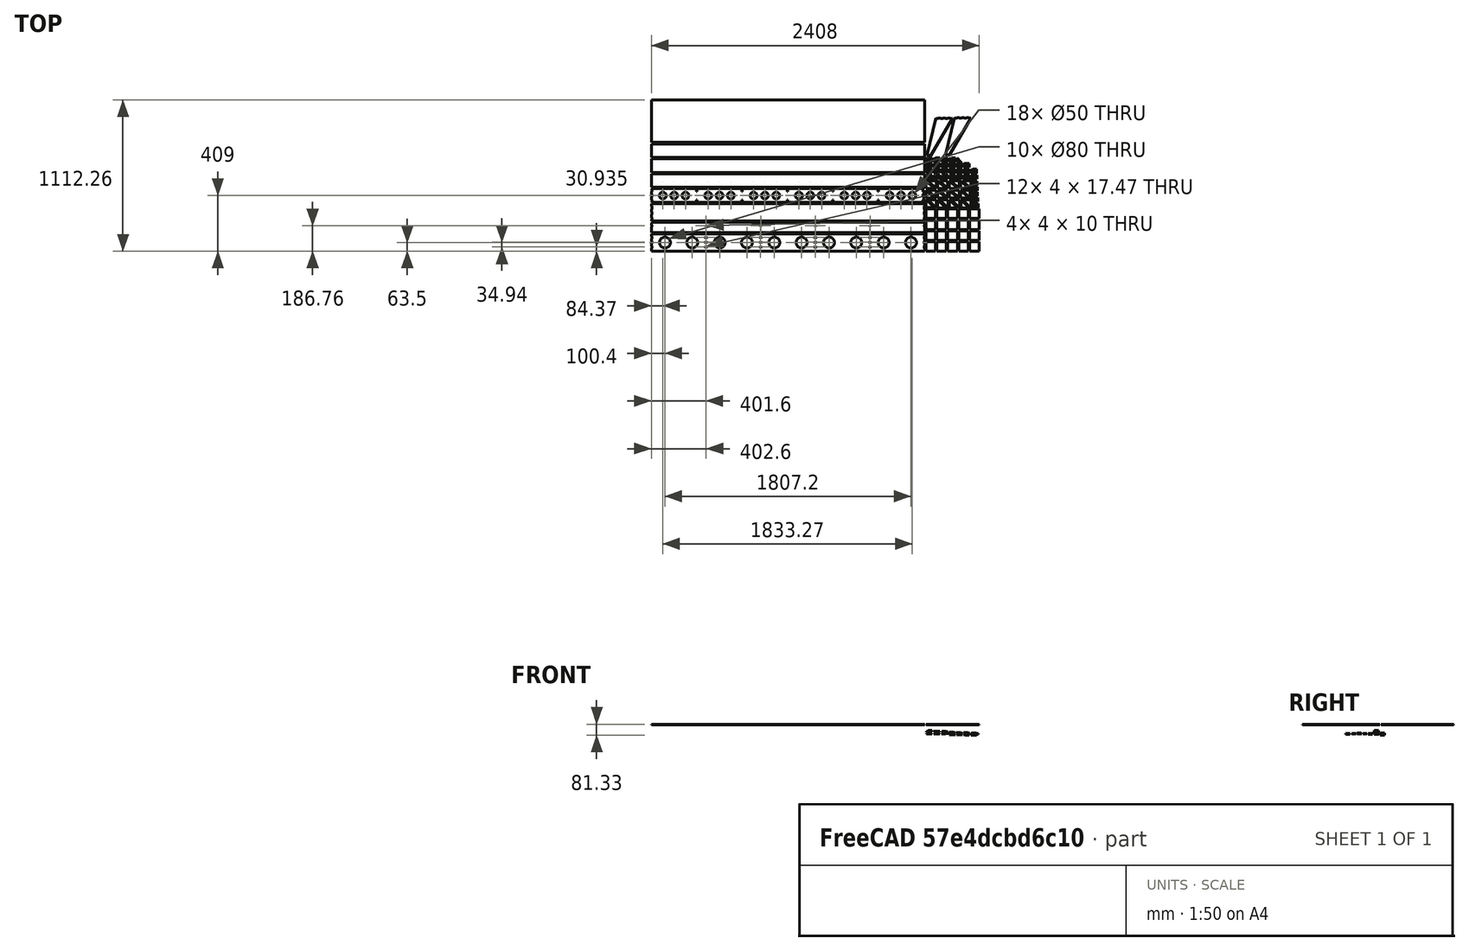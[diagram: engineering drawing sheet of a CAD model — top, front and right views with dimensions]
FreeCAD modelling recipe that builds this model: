
FCSTD DOCUMENT  (FreeCAD 0.19R24291 (Git))
Label: CAM-3
License: All rights reserved
LicenseURL: http://en.wikipedia.org/wiki/All_rights_reserved
objects: Part::Feature×113, Part::Part2DObjectPython×113
note: 226 computed .brp shape members not serialized (recipe doc carries the construction recipe); baked Part::Feature solids carry a one-line shape summary decoded from their .brp

FEATURE [Part::Feature] test
  Placement = pos=(2219,3712,34) rot=(0,1,0;3.14159rad)
  shape: bbox 60 x 60 x 4 mm, 5 faces (baked)
FEATURE [Part::Feature] test001
  Placement = pos=(2150,3712,34) rot=(0,1,0;3.14159rad)
  shape: bbox 60 x 60 x 4 mm, 5 faces (baked)
FEATURE [Part::Feature] test002
  Placement = pos=(2273,3782,34) rot=(0,1,0;3.14159rad)
  shape: bbox 60 x 60 x 4 mm, 5 faces (baked)
FEATURE [Part::Feature] test003
  Placement = pos=(2336,3782,34) rot=(0,1,0;3.14159rad)
  shape: bbox 60 x 60 x 4 mm, 5 faces (baked)
FEATURE [Part::Feature] test004
  Placement = pos=(2290,3852,34) rot=(0,1,0;3.14159rad)
  shape: bbox 60 x 60 x 4 mm, 5 faces (baked)
FEATURE [Part::Feature] test005
  Placement = pos=(2478,3852,34) rot=(0,1,0;3.14159rad)
  shape: bbox 60 x 60 x 4 mm, 5 faces (baked)
FEATURE [Part::Feature] test006
  Placement = pos=(2503,3852,34) rot=(0,1,0;3.14159rad)
  shape: bbox 60 x 60 x 4 mm, 5 faces (baked)
FEATURE [Part::Feature] test011
  Placement = pos=(2824,3712,34) rot=(0,1,0;3.14159rad)
  shape: bbox 60 x 60 x 4 mm, 5 faces (baked)
FEATURE [Part::Feature] test012
  Placement = pos=(3004,3712,34) rot=(0,1,0;3.14159rad)
  shape: bbox 60 x 60 x 4 mm, 5 faces (baked)
FEATURE [Part::Feature] test013
  Placement = pos=(2848,3782,34) rot=(0,1,0;3.14159rad)
  shape: bbox 60 x 60 x 4 mm, 5 faces (baked)
FEATURE [Part::Feature] test014
  Placement = pos=(3213,3782,34) rot=(0,1,0;3.14159rad)
  shape: bbox 60 x 60 x 4 mm, 5 faces (baked)
FEATURE [Part::Feature] test015
  Placement = pos=(3028,3782,34) rot=(0,1,0;3.14159rad)
  shape: bbox 60 x 60 x 4 mm, 5 faces (baked)
FEATURE [Part::Feature] test016
  Placement = pos=(2493,3852,34) rot=(0,1,0;3.14159rad)
  shape: bbox 60 x 60 x 4 mm, 5 faces (baked)
FEATURE [Part::Feature] test017
  Placement = pos=(3323,3852,34) rot=(0,1,0;3.14159rad)
  shape: bbox 60 x 60 x 4 mm, 5 faces (baked)
FEATURE [Part::Feature] test018
  Placement = pos=(3303,3782,34) rot=(0,1,0;3.14159rad)
  shape: bbox 60 x 60 x 4 mm, 5 faces (baked)
FEATURE [Part::Feature] test020
  Placement = pos=(3333,3852,34) rot=(0,1,0;3.14159rad)
  shape: bbox 60 x 60 x 4 mm, 5 faces (baked)
FEATURE [Part::Feature] test021
  Placement = pos=(3528,3852,34) rot=(0,1,0;3.14159rad)
  shape: bbox 60 x 60 x 4 mm, 5 faces (baked)
FEATURE [Part::Feature] test022
  Placement = pos=(3288,3713,34) rot=(0,1,0;3.14159rad)
  shape: bbox 60 x 60 x 4 mm, 5 faces (baked)
FEATURE [Part::Feature] test023
  Placement = pos=(3469,3712,34) rot=(0,1,0;3.14159rad)
  shape: bbox 60 x 60 x 4 mm, 5 faces (baked)
FEATURE [Part::Feature] test024
  Placement = pos=(3654,3712,34) rot=(0,1,0;3.14159rad)
  shape: bbox 60 x 60 x 4 mm, 5 faces (baked)
FEATURE [Part::Feature] test025
  Placement = pos=(3593,3782,34) rot=(0,1,0;3.14159rad)
  shape: bbox 60 x 60 x 4 mm, 5 faces (baked)
FEATURE [Part::Feature] test026
  Placement = pos=(3749,3712,34) rot=(0,1,0;3.14159rad)
  shape: bbox 60 x 60 x 4 mm, 5 faces (baked)
FEATURE [Part::Feature] test027
  Placement = pos=(3788,3852,34) rot=(0,1,0;3.14159rad)
  shape: bbox 60 x 60 x 4 mm, 5 faces (baked)
FEATURE [Part::Feature] test028
  Placement = pos=(3773,3782,34) rot=(0,1,0;3.14159rad)
  shape: bbox 60 x 60 x 4 mm, 5 faces (baked)
FEATURE [Part::Feature] test029
  Placement = pos=(2373,3738,34) rot=(0,1,0;3.14159rad)
  shape: bbox 70 x 70 x 4 mm, 6 faces (baked)
FEATURE [Part::Feature] test030
  Placement = pos=(2373,3598,34) rot=(0,1,0;3.14159rad)
  shape: bbox 70 x 70 x 4 mm, 6 faces (baked)
FEATURE [Part::Feature] test031
  Placement = pos=(2153,3578,34) rot=(0,1,0;3.14159rad)
  shape: bbox 70 x 70 x 4 mm, 6 faces (baked)
FEATURE [Part::Feature] test032
  Placement = pos=(2393,3598,34) rot=(0,1,0;3.14159rad)
  shape: bbox 70 x 70 x 4 mm, 6 faces (baked)
FEATURE [Part::Feature] test033
  Placement = pos=(2493,3578,34) rot=(0,1,0;3.14159rad)
  shape: bbox 70 x 70 x 4 mm, 6 faces (baked)
FEATURE [Part::Feature] test034
  Placement = pos=(2253,3758,34) rot=(0,1,0;3.14159rad)
  shape: bbox 70 x 70 x 4 mm, 6 faces (baked)
FEATURE [Part::Feature] test035
  Placement = pos=(2353,3838,34) rot=(0,1,0;3.14159rad)
  shape: bbox 70 x 70 x 4 mm, 6 faces (baked)
FEATURE [Part::Feature] test036
  Placement = pos=(2433,3738,34) rot=(0,1,0;3.14159rad)
  shape: bbox 70 x 70 x 4 mm, 6 faces (baked)
FEATURE [Part::Feature] test037
  Placement = pos=(2613,3838,34) rot=(0,1,0;3.14159rad)
  shape: bbox 70 x 70 x 4 mm, 6 faces (baked)
FEATURE [Part::Feature] test038
  Placement = pos=(2693,3738,34) rot=(0,1,0;3.14159rad)
  shape: bbox 70 x 70 x 4 mm, 6 faces (baked)
FEATURE [Part::Feature] test039
  Placement = pos=(2873,3578,34) rot=(0,1,0;3.14159rad)
  shape: bbox 70 x 70 x 4 mm, 6 faces (baked)
FEATURE [Part::Feature] test040
  Placement = pos=(2873,3758,34) rot=(0,1,0;3.14159rad)
  shape: bbox 70 x 70 x 4 mm, 6 faces (baked)
FEATURE [Part::Feature] test041
  Placement = pos=(2813,3498,34) rot=(0,1,0;3.14159rad)
  shape: bbox 70 x 70 x 4 mm, 6 faces (baked)
FEATURE [Part::Feature] test042
  Placement = pos=(2733,3598,34) rot=(0,1,0;3.14159rad)
  shape: bbox 70 x 70 x 4 mm, 6 faces (baked)
FEATURE [Part::Feature] test043
  Placement = pos=(2753,3598,34) rot=(0,1,0;3.14159rad)
  shape: bbox 70 x 70 x 4 mm, 6 faces (baked)
FEATURE [Part::Feature] test044
  Placement = pos=(2833,3578,34) rot=(0,1,0;3.14159rad)
  shape: bbox 70 x 70 x 4 mm, 6 faces (baked)
FEATURE [Part::Feature] test045
  Placement = pos=(3013,3678,34) rot=(0,1,0;3.14159rad)
  shape: bbox 70 x 70 x 4 mm, 6 faces (baked)
FEATURE [Part::Feature] test046
  Placement = pos=(2933,3658,34) rot=(0,1,0;3.14159rad)
  shape: bbox 70 x 70 x 4 mm, 6 faces (baked)
FEATURE [Part::Feature] test047
  Placement = pos=(3113,3758,34) rot=(0,1,0;3.14159rad)
  shape: bbox 70 x 70 x 4 mm, 6 faces (baked)
FEATURE [Part::Feature] test048
  Placement = pos=(3193,3658,34) rot=(0,1,0;3.14159rad)
  shape: bbox 70 x 70 x 4 mm, 6 faces (baked)
FEATURE [Part::Feature] test049
  Placement = pos=(2204.93,4207.11,-25.2046) rot=(0,1,0;3.14159rad)
  shape: bbox 30 x 30 x 4 mm, 5 faces (baked)
FEATURE [Part::Feature] test050
  Placement = pos=(2219.52,4207.19,-22.4733) rot=(0,1,0;3.14159rad)
  shape: bbox 30 x 30 x 4 mm, 5 faces (baked)
FEATURE [Part::Feature] test051
  Placement = pos=(2241.29,4206.7,-19.2967) rot=(0,1,0;3.14159rad)
  shape: bbox 30 x 30 x 4 mm, 5 faces (baked)
FEATURE [Part::Feature] test052
  Placement = pos=(2169.36,4207.86,-17.4437) rot=(0,1,0;3.14159rad)
  shape: bbox 30 x 30 x 4 mm, 5 faces (baked)
FEATURE [Part::Feature] test053
  Placement = pos=(2308.6,4207.73,-17.9467) rot=(0,1,0;3.14159rad)
  shape: bbox 30 x 30 x 4 mm, 5 faces (baked)
FEATURE [Part::Feature] test054
  Placement = pos=(2264.57,4207.49,-13.3782) rot=(0,1,0;3.14159rad)
  shape: bbox 30 x 30 x 4 mm, 5 faces (baked)
FEATURE [Part::Feature] test055
  Placement = pos=(2451.48,4252.87,-38.6741) rot=(0,1,0;3.14159rad)
  shape: bbox 30 x 30 x 4 mm, 5 faces (baked)
FEATURE [Part::Feature] test056
  Placement = pos=(2582.06,4251.78,-39.2106) rot=(0,1,0;3.14159rad)
  shape: bbox 30 x 30 x 4 mm, 5 faces (baked)
FEATURE [Part::Feature] test057
  Placement = pos=(2343.78,4293.17,34) rot=(0,1,0;3.14159rad)
  shape: bbox 30 x 30 x 4 mm, 5 faces (baked)
FEATURE [Part::Feature] test058
  Placement = pos=(2552.47,4294.85,34) rot=(0,1,0;3.14159rad)
  shape: bbox 30 x 30 x 4 mm, 5 faces (baked)
FEATURE [Part::Feature] test059
  Placement = pos=(2536.46,4294.85,34) rot=(0,1,0;3.14159rad)
  shape: bbox 30 x 30 x 4 mm, 5 faces (baked)
FEATURE [Part::Feature] test060
  Placement = pos=(2733.13,4294.85,34) rot=(0,1,0;3.14159rad)
  shape: bbox 30 x 30 x 4 mm, 5 faces (baked)
FEATURE [Part::Feature] test061
  Placement = pos=(2503.67,4333.51,34) rot=(0,1,0;3.14159rad)
  shape: bbox 30 x 30 x 4 mm, 5 faces (baked)
FEATURE [Part::Feature] test062
  Placement = pos=(2928.72,3997.69,-35.1689) rot=(0,1,0;3.14159rad)
  shape: bbox 30 x 30 x 4 mm, 5 faces (baked)
FEATURE [Part::Feature] test063
  Placement = pos=(2795.04,4207.57,-30.115) rot=(0,1,0;3.14159rad)
  shape: bbox 30 x 30 x 4 mm, 5 faces (baked)
FEATURE [Part::Feature] test064
  Placement = pos=(2824.34,4206.36,-27.0734) rot=(0,1,0;3.14159rad)
  shape: bbox 30 x 30 x 4 mm, 5 faces (baked)
FEATURE [Part::Feature] test065
  Placement = pos=(2811,4207.49,-26.9938) rot=(0,1,0;3.14159rad)
  shape: bbox 30 x 30 x 4 mm, 5 faces (baked)
FEATURE [Part::Feature] test066
  Placement = pos=(2904.44,4251.13,-39.2664) rot=(0,1,0;3.14159rad)
  shape: bbox 30 x 30 x 4 mm, 5 faces (baked)
FEATURE [Part::Feature] test067
  Placement = pos=(2945.14,4250.68,-41.0286) rot=(0,1,0;3.14159rad)
  shape: bbox 30 x 30 x 4 mm, 5 faces (baked)
FEATURE [Part::Feature] test068
  Placement = pos=(2789.78,4293.94,34) rot=(0,1,0;3.14159rad)
  shape: bbox 30 x 30 x 4 mm, 5 faces (baked)
FEATURE [Part::Feature] test069
  Placement = pos=(2839.32,4295.06,34) rot=(0,1,0;3.14159rad)
  shape: bbox 30 x 30 x 4 mm, 5 faces (baked)
FEATURE [Part::Feature] test070
  Placement = pos=(2973.24,4295.15,34) rot=(0,1,0;3.14159rad)
  shape: bbox 30 x 30 x 4 mm, 5 faces (baked)
FEATURE [Part::Feature] test071
  Placement = pos=(2738.02,4334.55,34) rot=(0,1,0;3.14159rad)
  shape: bbox 30 x 30 x 4 mm, 5 faces (baked)
FEATURE [Part::Feature] test072
  Placement = pos=(2874.75,4334.28,34) rot=(0,1,0;3.14159rad)
  shape: bbox 30 x 30 x 4 mm, 5 faces (baked)
FEATURE [Part::Feature] test073
  Placement = pos=(3224.21,3997.16,-35.6939) rot=(0,1,0;3.14159rad)
  shape: bbox 30 x 30 x 4 mm, 5 faces (baked)
FEATURE [Part::Feature] test074
  Placement = pos=(3236.81,4040.63,-33.7602) rot=(0,1,0;3.14159rad)
  shape: bbox 30 x 30 x 4 mm, 5 faces (baked)
FEATURE [Part::Feature] test075
  Placement = pos=(3242.01,4207.06,-30.7179) rot=(0,1,0;3.14159rad)
  shape: bbox 30 x 30 x 4 mm, 5 faces (baked)
FEATURE [Part::Feature] test076
  Placement = pos=(3255.03,4207.48,-28.8446) rot=(0,1,0;3.14159rad)
  shape: bbox 30 x 30 x 4 mm, 5 faces (baked)
FEATURE [Part::Feature] test077
  Placement = pos=(3258.08,4250.89,-41.0843) rot=(0,1,0;3.14159rad)
  shape: bbox 30 x 30 x 4 mm, 5 faces (baked)
FEATURE [Part::Feature] test078
  Placement = pos=(3390.73,4250.22,-41.5606) rot=(0,1,0;3.14159rad)
  shape: bbox 30 x 30 x 4 mm, 5 faces (baked)
FEATURE [Part::Feature] test079
  Placement = pos=(3387.34,4250.08,-41.5626) rot=(0,1,0;3.14159rad)
  shape: bbox 30 x 30 x 4 mm, 5 faces (baked)
FEATURE [Part::Feature] test080
  Placement = pos=(3193.91,4293.87,34) rot=(0,1,0;3.14159rad)
  shape: bbox 30 x 30 x 4 mm, 5 faces (baked)
FEATURE [Part::Feature] test081
  Placement = pos=(3469.53,4293.98,34) rot=(0,1,0;3.14159rad)
  shape: bbox 30 x 30 x 4 mm, 5 faces (baked)
FEATURE [Part::Feature] test082
  Placement = pos=(3332.54,4334.2,34) rot=(0,1,0;3.14159rad)
  shape: bbox 30 x 30 x 4 mm, 5 faces (baked)
FEATURE [Part::Feature] test083
  Placement = pos=(3333.65,4333.93,34) rot=(0,1,0;3.14159rad)
  shape: bbox 30 x 30 x 4 mm, 5 faces (baked)
FEATURE [Part::Feature] test084
  Placement = pos=(3685.99,4206.94,-35.222) rot=(0,1,0;3.14159rad)
  shape: bbox 30 x 30 x 4 mm, 5 faces (baked)
FEATURE [Part::Feature] test085
  Placement = pos=(3635.07,4123.66,-33.6609) rot=(0,1,0;3.14159rad)
  shape: bbox 30 x 30 x 4 mm, 5 faces (baked)
FEATURE [Part::Feature] test086
  Placement = pos=(3773.24,4041.85,-32.8391) rot=(0,1,0;3.14159rad)
  shape: bbox 30 x 30 x 4 mm, 5 faces (baked)
FEATURE [Part::Feature] test087
  Placement = pos=(3715.39,4080.71,-31.029) rot=(0,1,0;3.14159rad)
  shape: bbox 30 x 30 x 4 mm, 5 faces (baked)
FEATURE [Part::Feature] test088
  Placement = pos=(3459.34,4251.87,-32.9911) rot=(0,1,0;3.14159rad)
  shape: bbox 30 x 30 x 4 mm, 5 faces (baked)
FEATURE [Part::Feature] test089
  Placement = pos=(3844.41,4251.11,-43.3309) rot=(0,1,0;3.14159rad)
  shape: bbox 30 x 30 x 4 mm, 5 faces (baked)
FEATURE [Part::Feature] test090
  Placement = pos=(3538.86,4293.21,34) rot=(0,1,0;3.14159rad)
  shape: bbox 30 x 30 x 4 mm, 5 faces (baked)
FEATURE [Part::Feature] test091
  Placement = pos=(3818.42,4295.56,34) rot=(0,1,0;3.14159rad)
  shape: bbox 30 x 30 x 4 mm, 5 faces (baked)
FEATURE [Part::Feature] test092
  Placement = pos=(3894.39,4294.26,34) rot=(0,1,0;3.14159rad)
  shape: bbox 30 x 30 x 4 mm, 5 faces (baked)
FEATURE [Part::Feature] test093
  Placement = pos=(3850.15,4332.35,34) rot=(0,1,0;3.14159rad)
  shape: bbox 30 x 30 x 4 mm, 5 faces (baked)
FEATURE [Part::Feature] test094
  Placement = pos=(3869.81,4333.35,34) rot=(0,1,0;3.14159rad)
  shape: bbox 30 x 30 x 4 mm, 5 faces (baked)
FEATURE [Part::Feature] test095
  Placement = pos=(4086.62,4161.95,-35.224) rot=(0,1,0;3.14159rad)
  shape: bbox 30 x 30 x 4 mm, 5 faces (baked)
FEATURE [Part::Feature] test096
  Placement = pos=(4108.86,4207.4,-33.482) rot=(0,1,0;3.14159rad)
  shape: bbox 30 x 30 x 4 mm, 5 faces (baked)
FEATURE [Part::Feature] test097
  Placement = pos=(4170.9,4082.98,-32.7595) rot=(0,1,0;3.14159rad)
  shape: bbox 30 x 30 x 4 mm, 5 faces (baked)
FEATURE [Part::Feature] test098
  Placement = pos=(3859.82,4207.89,-19.66) rot=(0,1,0;3.14159rad)
  shape: bbox 30 x 30 x 4 mm, 5 faces (baked)
FEATURE [Part::Feature] test099
  Placement = pos=(3918.28,4251.35,-33.5551) rot=(0,1,0;3.14159rad)
  shape: bbox 30 x 30 x 4 mm, 5 faces (baked)
FEATURE [Part::Feature] test100
  Placement = pos=(3993.95,4252.01,-33.5112) rot=(0,1,0;3.14159rad)
  shape: bbox 30 x 30 x 4 mm, 5 faces (baked)
FEATURE [Part::Feature] test101
  Placement = pos=(4055.01,4252.2,-32.7736) rot=(0,1,0;3.14159rad)
  shape: bbox 30 x 30 x 4 mm, 5 faces (baked)
FEATURE [Part::Feature] test102
  Placement = pos=(4131.15,4253.38,-32.811) rot=(0,1,0;3.14159rad)
  shape: bbox 30 x 30 x 4 mm, 5 faces (baked)
FEATURE [Part::Feature] test103
  Placement = pos=(4191.09,4333.78,34) rot=(0,1,0;3.14159rad)
  shape: bbox 30 x 30 x 4 mm, 5 faces (baked)
FEATURE [Part::Feature] test104
  Placement = pos=(4271.05,4253.08,-30.6289) rot=(0,1,0;3.14159rad)
  shape: bbox 30 x 30 x 4 mm, 5 faces (baked)
FEATURE [Part::Feature] test105
  Placement = pos=(4326.29,4333.18,34) rot=(0,1,0;3.14159rad)
  shape: bbox 30 x 30 x 4 mm, 5 faces (baked)
FEATURE [Part::Feature] test106
  Placement = pos=(4514.02,4161.12,-35.008) rot=(0,1,0;3.14159rad)
  shape: bbox 30 x 30 x 4 mm, 5 faces (baked)
FEATURE [Part::Feature] test107
  Placement = pos=(4569.29,4122.33,-34.048) rot=(0,1,0;3.14159rad)
  shape: bbox 30 x 30 x 4 mm, 5 faces (baked)
FEATURE [Part::Feature] test108
  Placement = pos=(2009,4502,34) rot=(0,1,0;3.14159rad)
  shape: bbox 2008 x 100 x 4 mm, 6 faces (baked)
FEATURE [Part::Feature] test109
  Placement = pos=(2009,4392,34) rot=(0,1,0;3.14159rad)
  shape: bbox 2008 x 100 x 4 mm, 6 faces (baked)
FEATURE [Part::Feature] test110
  Placement = pos=(2009,4612,34) rot=(0,1,0;3.14159rad)
  shape: bbox 2008 x 100 x 4 mm, 6 faces (baked)
FEATURE [Part::Feature] test111
  Placement = pos=(1001,1059,-268) rot=(1,0,0;1.5708rad)
  shape: bbox 2000 x 100 x 4 mm, 80 faces (baked)
FEATURE [Part::Feature] test112
  Placement = pos=(1005,947,634) rot=(1,0,0;1.5708rad)
  shape: bbox 2008 x 127 x 4 mm, 30 faces (baked)
FEATURE [Part::Feature] test113
  Placement = pos=(2142.38,2233.25,-970) rot=(0,1,0;1.5708rad)
  shape: bbox 187.7 x 277.1 x 4 mm, 23 faces (baked)
FEATURE [Part::Feature] test114
  Placement = pos=(1004,725,638) rot=(1,0,0;1.5708rad)
  shape: bbox 2008 x 127 x 4 mm, 88 faces (baked)
FEATURE [Part::Feature] test115
  Placement = pos=(2279.6,2235.36,1034) rot=(0,1,0;1.5708rad)
  shape: bbox 187.7 x 277.1 x 4 mm, 23 faces (baked)
FEATURE [Part::Feature] test120
  Placement = pos=(1005,959,396.842) rot=(1,0,0;2.61799rad)
  shape: bbox 2008 x 313 x 4 mm, 6 faces (baked)
FEATURE [Part::Feature] test121
  Placement = pos=(1005,742,911.1) rot=(1,0,0;1.5708rad)
  shape: bbox 2008 x 74.7 x 4 mm, 50 faces (baked)
FEATURE [Part::Part2DObjectPython] Shape2DView  # Draft 2D object (typed FeaturePython)
  Base = -> test
  FuseArch = false
  HiddenLines = false
  InPlace = true
  Projection = (0,0,1)
  ProjectionMode = 0
  SegmentLength = 0.05
  Tessellation = false
  VisibleOnly = false
FEATURE [Part::Part2DObjectPython] Shape2DView001  # Draft 2D object (typed FeaturePython)
  Base = -> test001
  FuseArch = false
  HiddenLines = false
  InPlace = true
  Projection = (0,0,1)
  ProjectionMode = 0
  SegmentLength = 0.05
  Tessellation = false
  VisibleOnly = false
FEATURE [Part::Part2DObjectPython] Shape2DView002  # Draft 2D object (typed FeaturePython)
  Base = -> test002
  FuseArch = false
  HiddenLines = false
  InPlace = true
  Projection = (0,0,1)
  ProjectionMode = 0
  SegmentLength = 0.05
  Tessellation = false
  VisibleOnly = false
FEATURE [Part::Part2DObjectPython] Shape2DView003  # Draft 2D object (typed FeaturePython)
  Base = -> test003
  FuseArch = false
  HiddenLines = false
  InPlace = true
  Projection = (0,0,1)
  ProjectionMode = 0
  SegmentLength = 0.05
  Tessellation = false
  VisibleOnly = false
FEATURE [Part::Part2DObjectPython] Shape2DView004  # Draft 2D object (typed FeaturePython)
  Base = -> test004
  FuseArch = false
  HiddenLines = false
  InPlace = true
  Projection = (0,0,1)
  ProjectionMode = 0
  SegmentLength = 0.05
  Tessellation = false
  VisibleOnly = false
FEATURE [Part::Part2DObjectPython] Shape2DView005  # Draft 2D object (typed FeaturePython)
  Base = -> test005
  FuseArch = false
  HiddenLines = false
  InPlace = true
  Projection = (0,0,1)
  ProjectionMode = 0
  SegmentLength = 0.05
  Tessellation = false
  VisibleOnly = false
FEATURE [Part::Part2DObjectPython] Shape2DView006  # Draft 2D object (typed FeaturePython)
  Base = -> test006
  FuseArch = false
  HiddenLines = false
  InPlace = true
  Projection = (0,0,1)
  ProjectionMode = 0
  SegmentLength = 0.05
  Tessellation = false
  VisibleOnly = false
FEATURE [Part::Part2DObjectPython] Shape2DView011  # Draft 2D object (typed FeaturePython)
  Base = -> test011
  FuseArch = false
  HiddenLines = false
  InPlace = true
  Projection = (0,0,1)
  ProjectionMode = 0
  SegmentLength = 0.05
  Tessellation = false
  VisibleOnly = false
FEATURE [Part::Part2DObjectPython] Shape2DView012  # Draft 2D object (typed FeaturePython)
  Base = -> test012
  FuseArch = false
  HiddenLines = false
  InPlace = true
  Projection = (0,0,1)
  ProjectionMode = 0
  SegmentLength = 0.05
  Tessellation = false
  VisibleOnly = false
FEATURE [Part::Part2DObjectPython] Shape2DView013  # Draft 2D object (typed FeaturePython)
  Base = -> test013
  FuseArch = false
  HiddenLines = false
  InPlace = true
  Projection = (0,0,1)
  ProjectionMode = 0
  SegmentLength = 0.05
  Tessellation = false
  VisibleOnly = false
FEATURE [Part::Part2DObjectPython] Shape2DView014  # Draft 2D object (typed FeaturePython)
  Base = -> test014
  FuseArch = false
  HiddenLines = false
  InPlace = true
  Projection = (0,0,1)
  ProjectionMode = 0
  SegmentLength = 0.05
  Tessellation = false
  VisibleOnly = false
FEATURE [Part::Part2DObjectPython] Shape2DView015  # Draft 2D object (typed FeaturePython)
  Base = -> test015
  FuseArch = false
  HiddenLines = false
  InPlace = true
  Projection = (0,0,1)
  ProjectionMode = 0
  SegmentLength = 0.05
  Tessellation = false
  VisibleOnly = false
FEATURE [Part::Part2DObjectPython] Shape2DView016  # Draft 2D object (typed FeaturePython)
  Base = -> test016
  FuseArch = false
  HiddenLines = false
  InPlace = true
  Projection = (0,0,1)
  ProjectionMode = 0
  SegmentLength = 0.05
  Tessellation = false
  VisibleOnly = false
FEATURE [Part::Part2DObjectPython] Shape2DView017  # Draft 2D object (typed FeaturePython)
  Base = -> test017
  FuseArch = false
  HiddenLines = false
  InPlace = true
  Projection = (0,0,1)
  ProjectionMode = 0
  SegmentLength = 0.05
  Tessellation = false
  VisibleOnly = false
FEATURE [Part::Part2DObjectPython] Shape2DView018  # Draft 2D object (typed FeaturePython)
  Base = -> test018
  FuseArch = false
  HiddenLines = false
  InPlace = true
  Projection = (0,0,1)
  ProjectionMode = 0
  SegmentLength = 0.05
  Tessellation = false
  VisibleOnly = false
FEATURE [Part::Part2DObjectPython] Shape2DView020  # Draft 2D object (typed FeaturePython)
  Base = -> test020
  FuseArch = false
  HiddenLines = false
  InPlace = true
  Projection = (0,0,1)
  ProjectionMode = 0
  SegmentLength = 0.05
  Tessellation = false
  VisibleOnly = false
FEATURE [Part::Part2DObjectPython] Shape2DView021  # Draft 2D object (typed FeaturePython)
  Base = -> test021
  FuseArch = false
  HiddenLines = false
  InPlace = true
  Projection = (0,0,1)
  ProjectionMode = 0
  SegmentLength = 0.05
  Tessellation = false
  VisibleOnly = false
FEATURE [Part::Part2DObjectPython] Shape2DView022  # Draft 2D object (typed FeaturePython)
  Base = -> test022
  FuseArch = false
  HiddenLines = false
  InPlace = true
  Projection = (0,0,1)
  ProjectionMode = 0
  SegmentLength = 0.05
  Tessellation = false
  VisibleOnly = false
FEATURE [Part::Part2DObjectPython] Shape2DView023  # Draft 2D object (typed FeaturePython)
  Base = -> test023
  FuseArch = false
  HiddenLines = false
  InPlace = true
  Projection = (0,0,1)
  ProjectionMode = 0
  SegmentLength = 0.05
  Tessellation = false
  VisibleOnly = false
FEATURE [Part::Part2DObjectPython] Shape2DView024  # Draft 2D object (typed FeaturePython)
  Base = -> test024
  FuseArch = false
  HiddenLines = false
  InPlace = true
  Projection = (0,0,1)
  ProjectionMode = 0
  SegmentLength = 0.05
  Tessellation = false
  VisibleOnly = false
FEATURE [Part::Part2DObjectPython] Shape2DView025  # Draft 2D object (typed FeaturePython)
  Base = -> test025
  FuseArch = false
  HiddenLines = false
  InPlace = true
  Projection = (0,0,1)
  ProjectionMode = 0
  SegmentLength = 0.05
  Tessellation = false
  VisibleOnly = false
FEATURE [Part::Part2DObjectPython] Shape2DView026  # Draft 2D object (typed FeaturePython)
  Base = -> test026
  FuseArch = false
  HiddenLines = false
  InPlace = true
  Projection = (0,0,1)
  ProjectionMode = 0
  SegmentLength = 0.05
  Tessellation = false
  VisibleOnly = false
FEATURE [Part::Part2DObjectPython] Shape2DView027  # Draft 2D object (typed FeaturePython)
  Base = -> test027
  FuseArch = false
  HiddenLines = false
  InPlace = true
  Projection = (0,0,1)
  ProjectionMode = 0
  SegmentLength = 0.05
  Tessellation = false
  VisibleOnly = false
FEATURE [Part::Part2DObjectPython] Shape2DView028  # Draft 2D object (typed FeaturePython)
  Base = -> test028
  FuseArch = false
  HiddenLines = false
  InPlace = true
  Projection = (0,0,1)
  ProjectionMode = 0
  SegmentLength = 0.05
  Tessellation = false
  VisibleOnly = false
FEATURE [Part::Part2DObjectPython] Shape2DView029  # Draft 2D object (typed FeaturePython)
  Base = -> test029
  FuseArch = false
  HiddenLines = false
  InPlace = true
  Projection = (0,0,1)
  ProjectionMode = 0
  SegmentLength = 0.05
  Tessellation = false
  VisibleOnly = false
FEATURE [Part::Part2DObjectPython] Shape2DView030  # Draft 2D object (typed FeaturePython)
  Base = -> test030
  FuseArch = false
  HiddenLines = false
  InPlace = true
  Projection = (0,0,1)
  ProjectionMode = 0
  SegmentLength = 0.05
  Tessellation = false
  VisibleOnly = false
FEATURE [Part::Part2DObjectPython] Shape2DView031  # Draft 2D object (typed FeaturePython)
  Base = -> test031
  FuseArch = false
  HiddenLines = false
  InPlace = true
  Projection = (0,0,1)
  ProjectionMode = 0
  SegmentLength = 0.05
  Tessellation = false
  VisibleOnly = false
FEATURE [Part::Part2DObjectPython] Shape2DView032  # Draft 2D object (typed FeaturePython)
  Base = -> test032
  FuseArch = false
  HiddenLines = false
  InPlace = true
  Projection = (0,0,1)
  ProjectionMode = 0
  SegmentLength = 0.05
  Tessellation = false
  VisibleOnly = false
FEATURE [Part::Part2DObjectPython] Shape2DView033  # Draft 2D object (typed FeaturePython)
  Base = -> test033
  FuseArch = false
  HiddenLines = false
  InPlace = true
  Projection = (0,0,1)
  ProjectionMode = 0
  SegmentLength = 0.05
  Tessellation = false
  VisibleOnly = false
FEATURE [Part::Part2DObjectPython] Shape2DView034  # Draft 2D object (typed FeaturePython)
  Base = -> test034
  FuseArch = false
  HiddenLines = false
  InPlace = true
  Projection = (0,0,1)
  ProjectionMode = 0
  SegmentLength = 0.05
  Tessellation = false
  VisibleOnly = false
FEATURE [Part::Part2DObjectPython] Shape2DView035  # Draft 2D object (typed FeaturePython)
  Base = -> test035
  FuseArch = false
  HiddenLines = false
  InPlace = true
  Projection = (0,0,1)
  ProjectionMode = 0
  SegmentLength = 0.05
  Tessellation = false
  VisibleOnly = false
FEATURE [Part::Part2DObjectPython] Shape2DView036  # Draft 2D object (typed FeaturePython)
  Base = -> test036
  FuseArch = false
  HiddenLines = false
  InPlace = true
  Projection = (0,0,1)
  ProjectionMode = 0
  SegmentLength = 0.05
  Tessellation = false
  VisibleOnly = false
FEATURE [Part::Part2DObjectPython] Shape2DView037  # Draft 2D object (typed FeaturePython)
  Base = -> test037
  FuseArch = false
  HiddenLines = false
  InPlace = true
  Projection = (0,0,1)
  ProjectionMode = 0
  SegmentLength = 0.05
  Tessellation = false
  VisibleOnly = false
FEATURE [Part::Part2DObjectPython] Shape2DView038  # Draft 2D object (typed FeaturePython)
  Base = -> test038
  FuseArch = false
  HiddenLines = false
  InPlace = true
  Projection = (0,0,1)
  ProjectionMode = 0
  SegmentLength = 0.05
  Tessellation = false
  VisibleOnly = false
FEATURE [Part::Part2DObjectPython] Shape2DView039  # Draft 2D object (typed FeaturePython)
  Base = -> test039
  FuseArch = false
  HiddenLines = false
  InPlace = true
  Projection = (0,0,1)
  ProjectionMode = 0
  SegmentLength = 0.05
  Tessellation = false
  VisibleOnly = false
FEATURE [Part::Part2DObjectPython] Shape2DView040  # Draft 2D object (typed FeaturePython)
  Base = -> test040
  FuseArch = false
  HiddenLines = false
  InPlace = true
  Projection = (0,0,1)
  ProjectionMode = 0
  SegmentLength = 0.05
  Tessellation = false
  VisibleOnly = false
FEATURE [Part::Part2DObjectPython] Shape2DView041  # Draft 2D object (typed FeaturePython)
  Base = -> test041
  FuseArch = false
  HiddenLines = false
  InPlace = true
  Projection = (0,0,1)
  ProjectionMode = 0
  SegmentLength = 0.05
  Tessellation = false
  VisibleOnly = false
FEATURE [Part::Part2DObjectPython] Shape2DView042  # Draft 2D object (typed FeaturePython)
  Base = -> test042
  FuseArch = false
  HiddenLines = false
  InPlace = true
  Projection = (0,0,1)
  ProjectionMode = 0
  SegmentLength = 0.05
  Tessellation = false
  VisibleOnly = false
FEATURE [Part::Part2DObjectPython] Shape2DView043  # Draft 2D object (typed FeaturePython)
  Base = -> test043
  FuseArch = false
  HiddenLines = false
  InPlace = true
  Projection = (0,0,1)
  ProjectionMode = 0
  SegmentLength = 0.05
  Tessellation = false
  VisibleOnly = false
FEATURE [Part::Part2DObjectPython] Shape2DView044  # Draft 2D object (typed FeaturePython)
  Base = -> test044
  FuseArch = false
  HiddenLines = false
  InPlace = true
  Projection = (0,0,1)
  ProjectionMode = 0
  SegmentLength = 0.05
  Tessellation = false
  VisibleOnly = false
FEATURE [Part::Part2DObjectPython] Shape2DView045  # Draft 2D object (typed FeaturePython)
  Base = -> test045
  FuseArch = false
  HiddenLines = false
  InPlace = true
  Projection = (0,0,1)
  ProjectionMode = 0
  SegmentLength = 0.05
  Tessellation = false
  VisibleOnly = false
FEATURE [Part::Part2DObjectPython] Shape2DView046  # Draft 2D object (typed FeaturePython)
  Base = -> test046
  FuseArch = false
  HiddenLines = false
  InPlace = true
  Projection = (0,0,1)
  ProjectionMode = 0
  SegmentLength = 0.05
  Tessellation = false
  VisibleOnly = false
FEATURE [Part::Part2DObjectPython] Shape2DView047  # Draft 2D object (typed FeaturePython)
  Base = -> test047
  FuseArch = false
  HiddenLines = false
  InPlace = true
  Projection = (0,0,1)
  ProjectionMode = 0
  SegmentLength = 0.05
  Tessellation = false
  VisibleOnly = false
FEATURE [Part::Part2DObjectPython] Shape2DView048  # Draft 2D object (typed FeaturePython)
  Base = -> test048
  FuseArch = false
  HiddenLines = false
  InPlace = true
  Projection = (0,0,1)
  ProjectionMode = 0
  SegmentLength = 0.05
  Tessellation = false
  VisibleOnly = false
FEATURE [Part::Part2DObjectPython] Shape2DView049  # Draft 2D object (typed FeaturePython)
  Base = -> test049
  FuseArch = false
  HiddenLines = false
  InPlace = true
  Projection = (0,0,1)
  ProjectionMode = 0
  SegmentLength = 0.05
  Tessellation = false
  VisibleOnly = false
FEATURE [Part::Part2DObjectPython] Shape2DView050  # Draft 2D object (typed FeaturePython)
  Base = -> test050
  FuseArch = false
  HiddenLines = false
  InPlace = true
  Projection = (0,0,1)
  ProjectionMode = 0
  SegmentLength = 0.05
  Tessellation = false
  VisibleOnly = false
FEATURE [Part::Part2DObjectPython] Shape2DView051  # Draft 2D object (typed FeaturePython)
  Base = -> test051
  FuseArch = false
  HiddenLines = false
  InPlace = true
  Projection = (0,0,1)
  ProjectionMode = 0
  SegmentLength = 0.05
  Tessellation = false
  VisibleOnly = false
FEATURE [Part::Part2DObjectPython] Shape2DView052  # Draft 2D object (typed FeaturePython)
  Base = -> test052
  FuseArch = false
  HiddenLines = false
  InPlace = true
  Projection = (0,0,1)
  ProjectionMode = 0
  SegmentLength = 0.05
  Tessellation = false
  VisibleOnly = false
FEATURE [Part::Part2DObjectPython] Shape2DView053  # Draft 2D object (typed FeaturePython)
  Base = -> test053
  FuseArch = false
  HiddenLines = false
  InPlace = true
  Projection = (0,0,1)
  ProjectionMode = 0
  SegmentLength = 0.05
  Tessellation = false
  VisibleOnly = false
FEATURE [Part::Part2DObjectPython] Shape2DView054  # Draft 2D object (typed FeaturePython)
  Base = -> test054
  FuseArch = false
  HiddenLines = false
  InPlace = true
  Projection = (0,0,1)
  ProjectionMode = 0
  SegmentLength = 0.05
  Tessellation = false
  VisibleOnly = false
FEATURE [Part::Part2DObjectPython] Shape2DView055  # Draft 2D object (typed FeaturePython)
  Base = -> test055
  FuseArch = false
  HiddenLines = false
  InPlace = true
  Projection = (0,0,1)
  ProjectionMode = 0
  SegmentLength = 0.05
  Tessellation = false
  VisibleOnly = false
FEATURE [Part::Part2DObjectPython] Shape2DView056  # Draft 2D object (typed FeaturePython)
  Base = -> test056
  FuseArch = false
  HiddenLines = false
  InPlace = true
  Projection = (0,0,1)
  ProjectionMode = 0
  SegmentLength = 0.05
  Tessellation = false
  VisibleOnly = false
FEATURE [Part::Part2DObjectPython] Shape2DView057  # Draft 2D object (typed FeaturePython)
  Base = -> test057
  FuseArch = false
  HiddenLines = false
  InPlace = true
  Projection = (0,0,1)
  ProjectionMode = 0
  SegmentLength = 0.05
  Tessellation = false
  VisibleOnly = false
FEATURE [Part::Part2DObjectPython] Shape2DView058  # Draft 2D object (typed FeaturePython)
  Base = -> test058
  FuseArch = false
  HiddenLines = false
  InPlace = true
  Projection = (0,0,1)
  ProjectionMode = 0
  SegmentLength = 0.05
  Tessellation = false
  VisibleOnly = false
FEATURE [Part::Part2DObjectPython] Shape2DView059  # Draft 2D object (typed FeaturePython)
  Base = -> test059
  FuseArch = false
  HiddenLines = false
  InPlace = true
  Projection = (0,0,1)
  ProjectionMode = 0
  SegmentLength = 0.05
  Tessellation = false
  VisibleOnly = false
FEATURE [Part::Part2DObjectPython] Shape2DView060  # Draft 2D object (typed FeaturePython)
  Base = -> test060
  FuseArch = false
  HiddenLines = false
  InPlace = true
  Projection = (0,0,1)
  ProjectionMode = 0
  SegmentLength = 0.05
  Tessellation = false
  VisibleOnly = false
FEATURE [Part::Part2DObjectPython] Shape2DView061  # Draft 2D object (typed FeaturePython)
  Base = -> test061
  FuseArch = false
  HiddenLines = false
  InPlace = true
  Projection = (0,0,1)
  ProjectionMode = 0
  SegmentLength = 0.05
  Tessellation = false
  VisibleOnly = false
FEATURE [Part::Part2DObjectPython] Shape2DView062  # Draft 2D object (typed FeaturePython)
  Base = -> test062
  FuseArch = false
  HiddenLines = false
  InPlace = true
  Projection = (0,0,1)
  ProjectionMode = 0
  SegmentLength = 0.05
  Tessellation = false
  VisibleOnly = false
FEATURE [Part::Part2DObjectPython] Shape2DView063  # Draft 2D object (typed FeaturePython)
  Base = -> test063
  FuseArch = false
  HiddenLines = false
  InPlace = true
  Projection = (0,0,1)
  ProjectionMode = 0
  SegmentLength = 0.05
  Tessellation = false
  VisibleOnly = false
FEATURE [Part::Part2DObjectPython] Shape2DView064  # Draft 2D object (typed FeaturePython)
  Base = -> test064
  FuseArch = false
  HiddenLines = false
  InPlace = true
  Projection = (0,0,1)
  ProjectionMode = 0
  SegmentLength = 0.05
  Tessellation = false
  VisibleOnly = false
FEATURE [Part::Part2DObjectPython] Shape2DView065  # Draft 2D object (typed FeaturePython)
  Base = -> test065
  FuseArch = false
  HiddenLines = false
  InPlace = true
  Projection = (0,0,1)
  ProjectionMode = 0
  SegmentLength = 0.05
  Tessellation = false
  VisibleOnly = false
FEATURE [Part::Part2DObjectPython] Shape2DView066  # Draft 2D object (typed FeaturePython)
  Base = -> test066
  FuseArch = false
  HiddenLines = false
  InPlace = true
  Projection = (0,0,1)
  ProjectionMode = 0
  SegmentLength = 0.05
  Tessellation = false
  VisibleOnly = false
FEATURE [Part::Part2DObjectPython] Shape2DView067  # Draft 2D object (typed FeaturePython)
  Base = -> test067
  FuseArch = false
  HiddenLines = false
  InPlace = true
  Projection = (0,0,1)
  ProjectionMode = 0
  SegmentLength = 0.05
  Tessellation = false
  VisibleOnly = false
FEATURE [Part::Part2DObjectPython] Shape2DView068  # Draft 2D object (typed FeaturePython)
  Base = -> test068
  FuseArch = false
  HiddenLines = false
  InPlace = true
  Projection = (0,0,1)
  ProjectionMode = 0
  SegmentLength = 0.05
  Tessellation = false
  VisibleOnly = false
FEATURE [Part::Part2DObjectPython] Shape2DView069  # Draft 2D object (typed FeaturePython)
  Base = -> test069
  FuseArch = false
  HiddenLines = false
  InPlace = true
  Projection = (0,0,1)
  ProjectionMode = 0
  SegmentLength = 0.05
  Tessellation = false
  VisibleOnly = false
FEATURE [Part::Part2DObjectPython] Shape2DView070  # Draft 2D object (typed FeaturePython)
  Base = -> test070
  FuseArch = false
  HiddenLines = false
  InPlace = true
  Projection = (0,0,1)
  ProjectionMode = 0
  SegmentLength = 0.05
  Tessellation = false
  VisibleOnly = false
FEATURE [Part::Part2DObjectPython] Shape2DView071  # Draft 2D object (typed FeaturePython)
  Base = -> test071
  FuseArch = false
  HiddenLines = false
  InPlace = true
  Projection = (0,0,1)
  ProjectionMode = 0
  SegmentLength = 0.05
  Tessellation = false
  VisibleOnly = false
FEATURE [Part::Part2DObjectPython] Shape2DView072  # Draft 2D object (typed FeaturePython)
  Base = -> test072
  FuseArch = false
  HiddenLines = false
  InPlace = true
  Projection = (0,0,1)
  ProjectionMode = 0
  SegmentLength = 0.05
  Tessellation = false
  VisibleOnly = false
FEATURE [Part::Part2DObjectPython] Shape2DView073  # Draft 2D object (typed FeaturePython)
  Base = -> test073
  FuseArch = false
  HiddenLines = false
  InPlace = true
  Projection = (0,0,1)
  ProjectionMode = 0
  SegmentLength = 0.05
  Tessellation = false
  VisibleOnly = false
FEATURE [Part::Part2DObjectPython] Shape2DView074  # Draft 2D object (typed FeaturePython)
  Base = -> test074
  FuseArch = false
  HiddenLines = false
  InPlace = true
  Projection = (0,0,1)
  ProjectionMode = 0
  SegmentLength = 0.05
  Tessellation = false
  VisibleOnly = false
FEATURE [Part::Part2DObjectPython] Shape2DView075  # Draft 2D object (typed FeaturePython)
  Base = -> test075
  FuseArch = false
  HiddenLines = false
  InPlace = true
  Projection = (0,0,1)
  ProjectionMode = 0
  SegmentLength = 0.05
  Tessellation = false
  VisibleOnly = false
FEATURE [Part::Part2DObjectPython] Shape2DView076  # Draft 2D object (typed FeaturePython)
  Base = -> test076
  FuseArch = false
  HiddenLines = false
  InPlace = true
  Projection = (0,0,1)
  ProjectionMode = 0
  SegmentLength = 0.05
  Tessellation = false
  VisibleOnly = false
FEATURE [Part::Part2DObjectPython] Shape2DView077  # Draft 2D object (typed FeaturePython)
  Base = -> test077
  FuseArch = false
  HiddenLines = false
  InPlace = true
  Projection = (0,0,1)
  ProjectionMode = 0
  SegmentLength = 0.05
  Tessellation = false
  VisibleOnly = false
FEATURE [Part::Part2DObjectPython] Shape2DView078  # Draft 2D object (typed FeaturePython)
  Base = -> test078
  FuseArch = false
  HiddenLines = false
  InPlace = true
  Projection = (0,0,1)
  ProjectionMode = 0
  SegmentLength = 0.05
  Tessellation = false
  VisibleOnly = false
FEATURE [Part::Part2DObjectPython] Shape2DView079  # Draft 2D object (typed FeaturePython)
  Base = -> test079
  FuseArch = false
  HiddenLines = false
  InPlace = true
  Projection = (0,0,1)
  ProjectionMode = 0
  SegmentLength = 0.05
  Tessellation = false
  VisibleOnly = false
FEATURE [Part::Part2DObjectPython] Shape2DView080  # Draft 2D object (typed FeaturePython)
  Base = -> test080
  FuseArch = false
  HiddenLines = false
  InPlace = true
  Projection = (0,0,1)
  ProjectionMode = 0
  SegmentLength = 0.05
  Tessellation = false
  VisibleOnly = false
FEATURE [Part::Part2DObjectPython] Shape2DView081  # Draft 2D object (typed FeaturePython)
  Base = -> test081
  FuseArch = false
  HiddenLines = false
  InPlace = true
  Projection = (0,0,1)
  ProjectionMode = 0
  SegmentLength = 0.05
  Tessellation = false
  VisibleOnly = false
FEATURE [Part::Part2DObjectPython] Shape2DView082  # Draft 2D object (typed FeaturePython)
  Base = -> test082
  FuseArch = false
  HiddenLines = false
  InPlace = true
  Projection = (0,0,1)
  ProjectionMode = 0
  SegmentLength = 0.05
  Tessellation = false
  VisibleOnly = false
FEATURE [Part::Part2DObjectPython] Shape2DView083  # Draft 2D object (typed FeaturePython)
  Base = -> test083
  FuseArch = false
  HiddenLines = false
  InPlace = true
  Projection = (0,0,1)
  ProjectionMode = 0
  SegmentLength = 0.05
  Tessellation = false
  VisibleOnly = false
FEATURE [Part::Part2DObjectPython] Shape2DView084  # Draft 2D object (typed FeaturePython)
  Base = -> test084
  FuseArch = false
  HiddenLines = false
  InPlace = true
  Projection = (0,0,1)
  ProjectionMode = 0
  SegmentLength = 0.05
  Tessellation = false
  VisibleOnly = false
FEATURE [Part::Part2DObjectPython] Shape2DView085  # Draft 2D object (typed FeaturePython)
  Base = -> test085
  FuseArch = false
  HiddenLines = false
  InPlace = true
  Projection = (0,0,1)
  ProjectionMode = 0
  SegmentLength = 0.05
  Tessellation = false
  VisibleOnly = false
FEATURE [Part::Part2DObjectPython] Shape2DView086  # Draft 2D object (typed FeaturePython)
  Base = -> test086
  FuseArch = false
  HiddenLines = false
  InPlace = true
  Projection = (0,0,1)
  ProjectionMode = 0
  SegmentLength = 0.05
  Tessellation = false
  VisibleOnly = false
FEATURE [Part::Part2DObjectPython] Shape2DView087  # Draft 2D object (typed FeaturePython)
  Base = -> test087
  FuseArch = false
  HiddenLines = false
  InPlace = true
  Projection = (0,0,1)
  ProjectionMode = 0
  SegmentLength = 0.05
  Tessellation = false
  VisibleOnly = false
FEATURE [Part::Part2DObjectPython] Shape2DView088  # Draft 2D object (typed FeaturePython)
  Base = -> test088
  FuseArch = false
  HiddenLines = false
  InPlace = true
  Projection = (0,0,1)
  ProjectionMode = 0
  SegmentLength = 0.05
  Tessellation = false
  VisibleOnly = false
FEATURE [Part::Part2DObjectPython] Shape2DView089  # Draft 2D object (typed FeaturePython)
  Base = -> test089
  FuseArch = false
  HiddenLines = false
  InPlace = true
  Projection = (0,0,1)
  ProjectionMode = 0
  SegmentLength = 0.05
  Tessellation = false
  VisibleOnly = false
FEATURE [Part::Part2DObjectPython] Shape2DView090  # Draft 2D object (typed FeaturePython)
  Base = -> test090
  FuseArch = false
  HiddenLines = false
  InPlace = true
  Projection = (0,0,1)
  ProjectionMode = 0
  SegmentLength = 0.05
  Tessellation = false
  VisibleOnly = false
FEATURE [Part::Part2DObjectPython] Shape2DView091  # Draft 2D object (typed FeaturePython)
  Base = -> test091
  FuseArch = false
  HiddenLines = false
  InPlace = true
  Projection = (0,0,1)
  ProjectionMode = 0
  SegmentLength = 0.05
  Tessellation = false
  VisibleOnly = false
FEATURE [Part::Part2DObjectPython] Shape2DView092  # Draft 2D object (typed FeaturePython)
  Base = -> test092
  FuseArch = false
  HiddenLines = false
  InPlace = true
  Projection = (0,0,1)
  ProjectionMode = 0
  SegmentLength = 0.05
  Tessellation = false
  VisibleOnly = false
FEATURE [Part::Part2DObjectPython] Shape2DView093  # Draft 2D object (typed FeaturePython)
  Base = -> test093
  FuseArch = false
  HiddenLines = false
  InPlace = true
  Projection = (0,0,1)
  ProjectionMode = 0
  SegmentLength = 0.05
  Tessellation = false
  VisibleOnly = false
FEATURE [Part::Part2DObjectPython] Shape2DView094  # Draft 2D object (typed FeaturePython)
  Base = -> test094
  FuseArch = false
  HiddenLines = false
  InPlace = true
  Projection = (0,0,1)
  ProjectionMode = 0
  SegmentLength = 0.05
  Tessellation = false
  VisibleOnly = false
FEATURE [Part::Part2DObjectPython] Shape2DView095  # Draft 2D object (typed FeaturePython)
  Base = -> test095
  FuseArch = false
  HiddenLines = false
  InPlace = true
  Projection = (0,0,1)
  ProjectionMode = 0
  SegmentLength = 0.05
  Tessellation = false
  VisibleOnly = false
FEATURE [Part::Part2DObjectPython] Shape2DView096  # Draft 2D object (typed FeaturePython)
  Base = -> test096
  FuseArch = false
  HiddenLines = false
  InPlace = true
  Projection = (0,0,1)
  ProjectionMode = 0
  SegmentLength = 0.05
  Tessellation = false
  VisibleOnly = false
FEATURE [Part::Part2DObjectPython] Shape2DView097  # Draft 2D object (typed FeaturePython)
  Base = -> test097
  FuseArch = false
  HiddenLines = false
  InPlace = true
  Projection = (0,0,1)
  ProjectionMode = 0
  SegmentLength = 0.05
  Tessellation = false
  VisibleOnly = false
FEATURE [Part::Part2DObjectPython] Shape2DView098  # Draft 2D object (typed FeaturePython)
  Base = -> test098
  FuseArch = false
  HiddenLines = false
  InPlace = true
  Projection = (0,0,1)
  ProjectionMode = 0
  SegmentLength = 0.05
  Tessellation = false
  VisibleOnly = false
FEATURE [Part::Part2DObjectPython] Shape2DView099  # Draft 2D object (typed FeaturePython)
  Base = -> test099
  FuseArch = false
  HiddenLines = false
  InPlace = true
  Projection = (0,0,1)
  ProjectionMode = 0
  SegmentLength = 0.05
  Tessellation = false
  VisibleOnly = false
FEATURE [Part::Part2DObjectPython] Shape2DView100  # Draft 2D object (typed FeaturePython)
  Base = -> test100
  FuseArch = false
  HiddenLines = false
  InPlace = true
  Projection = (0,0,1)
  ProjectionMode = 0
  SegmentLength = 0.05
  Tessellation = false
  VisibleOnly = false
FEATURE [Part::Part2DObjectPython] Shape2DView101  # Draft 2D object (typed FeaturePython)
  Base = -> test101
  FuseArch = false
  HiddenLines = false
  InPlace = true
  Projection = (0,0,1)
  ProjectionMode = 0
  SegmentLength = 0.05
  Tessellation = false
  VisibleOnly = false
FEATURE [Part::Part2DObjectPython] Shape2DView102  # Draft 2D object (typed FeaturePython)
  Base = -> test102
  FuseArch = false
  HiddenLines = false
  InPlace = true
  Projection = (0,0,1)
  ProjectionMode = 0
  SegmentLength = 0.05
  Tessellation = false
  VisibleOnly = false
FEATURE [Part::Part2DObjectPython] Shape2DView103  # Draft 2D object (typed FeaturePython)
  Base = -> test103
  FuseArch = false
  HiddenLines = false
  InPlace = true
  Projection = (0,0,1)
  ProjectionMode = 0
  SegmentLength = 0.05
  Tessellation = false
  VisibleOnly = false
FEATURE [Part::Part2DObjectPython] Shape2DView104  # Draft 2D object (typed FeaturePython)
  Base = -> test104
  FuseArch = false
  HiddenLines = false
  InPlace = true
  Projection = (0,0,1)
  ProjectionMode = 0
  SegmentLength = 0.05
  Tessellation = false
  VisibleOnly = false
FEATURE [Part::Part2DObjectPython] Shape2DView105  # Draft 2D object (typed FeaturePython)
  Base = -> test105
  FuseArch = false
  HiddenLines = false
  InPlace = true
  Projection = (0,0,1)
  ProjectionMode = 0
  SegmentLength = 0.05
  Tessellation = false
  VisibleOnly = false
FEATURE [Part::Part2DObjectPython] Shape2DView106  # Draft 2D object (typed FeaturePython)
  Base = -> test106
  FuseArch = false
  HiddenLines = false
  InPlace = true
  Projection = (0,0,1)
  ProjectionMode = 0
  SegmentLength = 0.05
  Tessellation = false
  VisibleOnly = false
FEATURE [Part::Part2DObjectPython] Shape2DView107  # Draft 2D object (typed FeaturePython)
  Base = -> test107
  FuseArch = false
  HiddenLines = false
  InPlace = true
  Projection = (0,0,1)
  ProjectionMode = 0
  SegmentLength = 0.05
  Tessellation = false
  VisibleOnly = false
FEATURE [Part::Part2DObjectPython] Shape2DView108  # Draft 2D object (typed FeaturePython)
  Base = -> test108
  FuseArch = false
  HiddenLines = false
  InPlace = true
  Projection = (0,0,1)
  ProjectionMode = 0
  SegmentLength = 0.05
  Tessellation = false
  VisibleOnly = false
FEATURE [Part::Part2DObjectPython] Shape2DView109  # Draft 2D object (typed FeaturePython)
  Base = -> test109
  FuseArch = false
  HiddenLines = false
  InPlace = true
  Projection = (0,0,1)
  ProjectionMode = 0
  SegmentLength = 0.05
  Tessellation = false
  VisibleOnly = false
FEATURE [Part::Part2DObjectPython] Shape2DView110  # Draft 2D object (typed FeaturePython)
  Base = -> test110
  FuseArch = false
  HiddenLines = false
  InPlace = true
  Projection = (0,0,1)
  ProjectionMode = 0
  SegmentLength = 0.05
  Tessellation = false
  VisibleOnly = false
FEATURE [Part::Part2DObjectPython] Shape2DView111  # Draft 2D object (typed FeaturePython)
  Base = -> test111
  FuseArch = false
  HiddenLines = false
  InPlace = true
  Projection = (0,0,1)
  ProjectionMode = 0
  SegmentLength = 0.05
  Tessellation = false
  VisibleOnly = false
FEATURE [Part::Part2DObjectPython] Shape2DView112  # Draft 2D object (typed FeaturePython)
  Base = -> test112
  FuseArch = false
  HiddenLines = false
  InPlace = true
  Projection = (0,0,1)
  ProjectionMode = 0
  SegmentLength = 0.05
  Tessellation = false
  VisibleOnly = false
FEATURE [Part::Part2DObjectPython] Shape2DView113  # Draft 2D object (typed FeaturePython)
  Base = -> test113
  FuseArch = false
  HiddenLines = false
  InPlace = true
  Projection = (0,0,1)
  ProjectionMode = 0
  SegmentLength = 0.05
  Tessellation = false
  VisibleOnly = false
FEATURE [Part::Part2DObjectPython] Shape2DView114  # Draft 2D object (typed FeaturePython)
  Base = -> test114
  FuseArch = false
  HiddenLines = false
  InPlace = true
  Projection = (0,0,1)
  ProjectionMode = 0
  SegmentLength = 0.05
  Tessellation = false
  VisibleOnly = false
FEATURE [Part::Part2DObjectPython] Shape2DView115  # Draft 2D object (typed FeaturePython)
  Base = -> test115
  FuseArch = false
  HiddenLines = false
  InPlace = true
  Projection = (0,0,1)
  ProjectionMode = 0
  SegmentLength = 0.05
  Tessellation = false
  VisibleOnly = false
FEATURE [Part::Part2DObjectPython] Shape2DView120  # Draft 2D object (typed FeaturePython)
  Base = -> test120
  FuseArch = false
  HiddenLines = false
  InPlace = true
  Projection = (0,0,1)
  ProjectionMode = 0
  SegmentLength = 0.05
  Tessellation = false
  VisibleOnly = false
FEATURE [Part::Part2DObjectPython] Shape2DView121  # Draft 2D object (typed FeaturePython)
  Base = -> test121
  FuseArch = false
  HiddenLines = false
  InPlace = true
  Projection = (0,0,1)
  ProjectionMode = 0
  SegmentLength = 0.05
  Tessellation = false
  VisibleOnly = false
